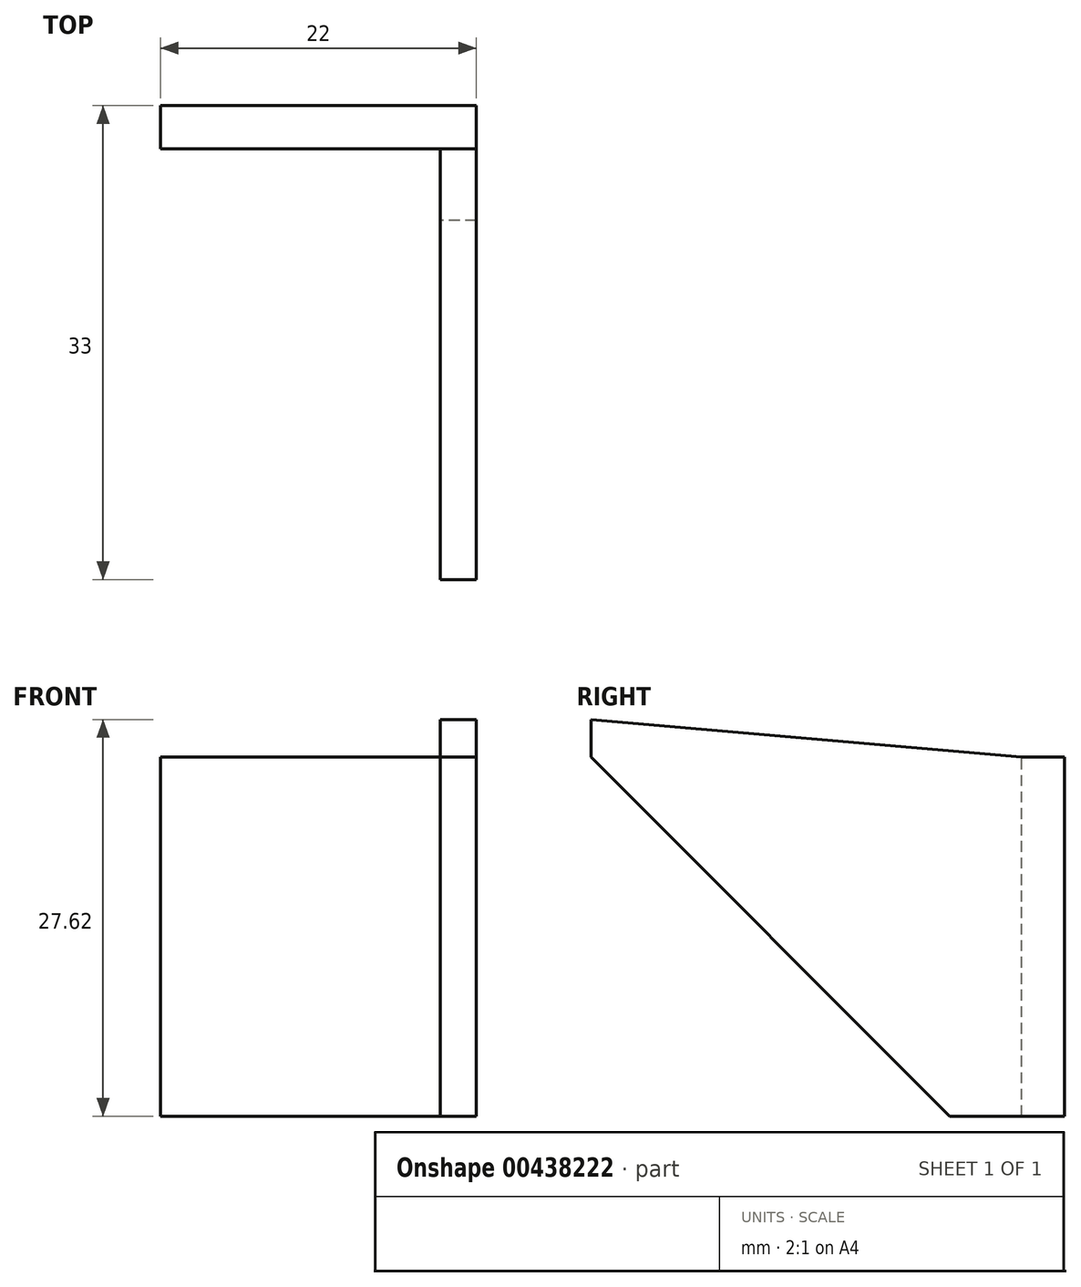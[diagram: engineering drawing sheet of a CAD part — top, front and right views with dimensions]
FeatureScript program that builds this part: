
annotation { "Feature Type Name" : "Feature", "Feature Type Description" : "" }
export const myFeature = defineFeature(function(context is Context, id is Id, definition is map)
    precondition{}
    {
        {
            var Q0;
            Q0=qCreatedBy(makeId("Front.planeOp"),FACE);
            var sketch = newSketch(context, id + "F0", { "sketchPlane" : qUnion([Q0])});
            skLineSegment(sketch, "E0.bottom", {"start": v(11, -12.5) * mm, "end": v(-11, -12.5) * mm});
            skLineSegment(sketch, "E0.top", {"start": v(11, 12.5) * mm, "end": v(-11, 12.5) * mm});
            skLineSegment(sketch, "E0.left", {"start": v(11, -12.5) * mm, "end": v(11, 12.5) * mm});
            skLineSegment(sketch, "E0.right", {"start": v(-11, -12.5) * mm, "end": v(-11, 12.5) * mm});
            skPoint(sketch, "E0.middle", {"position": v(0, 0) * mm});
            skSolve(sketch);
        }
        {
            var Q0;
            Q0=makeQuery(id+"F0.imprint","IMPRINT",FACE,{"disambiguationData":[TD([[makeQuery(id+"F0.imprint","IMPRINT",EDGE,{"derivedFrom":sQuery(id+"F0.wireOp",EDGE,"E0.bottom")}),-1.0]])]});
            extrude(context, id + "F1", {"entities" : qUnion([Q0]), "depth" : 3 * mm});
        }
        {
            var Q0;
            Q0=makeQuery(id+"F1.opExtrude","SWEPT_FACE",FACE,{"disambiguationData":[OSD([sQuery(id+"F0.wireOp",EDGE,"E0.left")])]});
            var sketch = newSketch(context, id + "F2", { "sketchPlane" : qUnion([Q0])});
            skLineSegment(sketch, "E1", {"start": v(-3, 12.5) * mm, "end": v(-33, 15.12) * mm});
            skLineSegment(sketch, "E2", {"start": v(-33, 15.12) * mm, "end": v(-33, -12.5) * mm});
            skLineSegment(sketch, "E3", {"start": v(-33, -12.5) * mm, "end": v(-3, -12.5) * mm});
            skLineSegment(sketch, "E4", {"start": v(-3, -12.5) * mm, "end": v(-3, 12.5) * mm});
            skSolve(sketch);
        }
        {
            var Q0;
            Q0 = qSketchRegion(id + "F2", true);
            extrude(context, id + "F3", {"entities" : qUnion([Q0]), "operationType" : NewBodyOperationType.ADD, "oppositeDirection" : true, "depth" : 2.5 * mm});
        }
        {
            var Q0;
            Q0=makeQuery(id+"F3.opExtrude","SWEPT_EDGE",EDGE,{"disambiguationData":[OSD([sQuery(id+"F2.wireOp",EDGE,"E2"),sQuery(id+"F2.wireOp",EDGE,"E3")])]});
            chamfer(context, id + "F4", {"entities" : qUnion([Q0]), "width" : 25 * mm, "tangentPropagation" : true});
        }
    });
